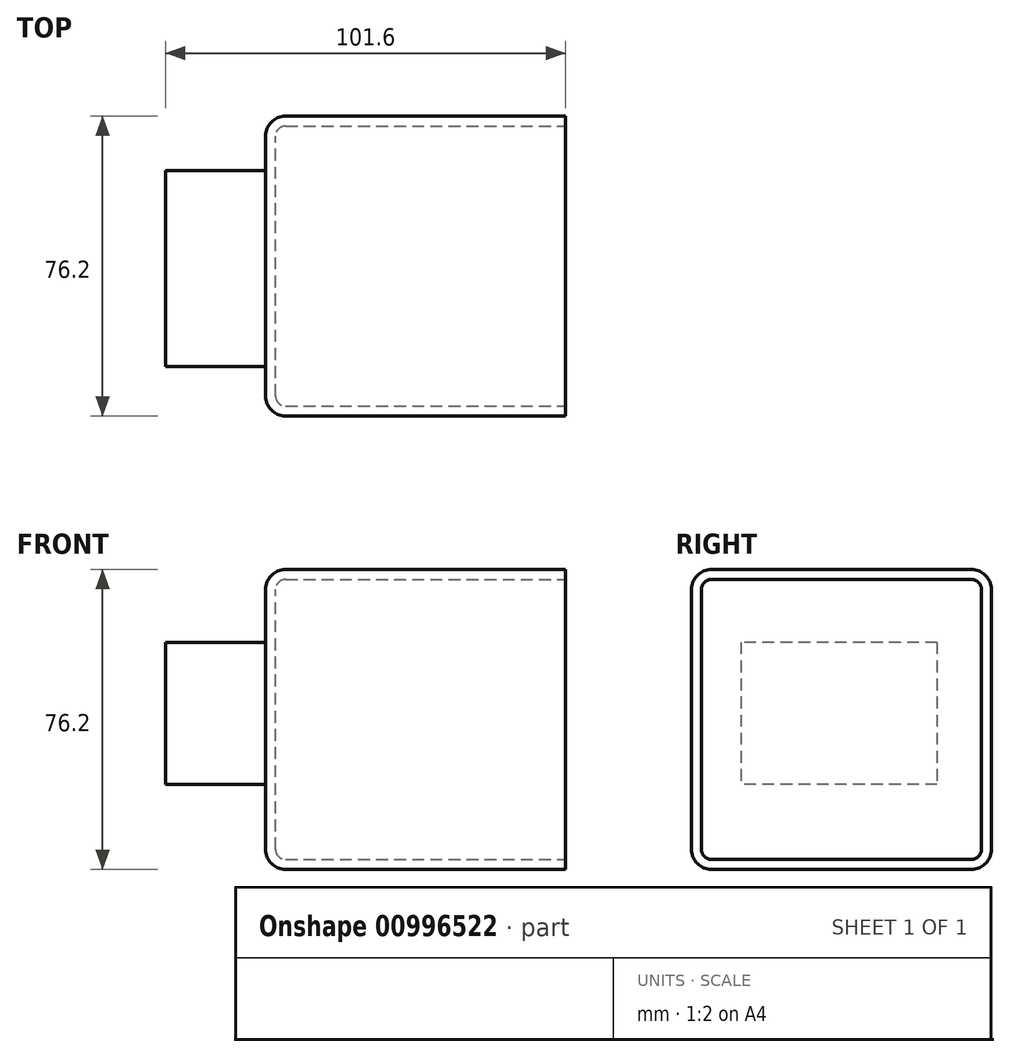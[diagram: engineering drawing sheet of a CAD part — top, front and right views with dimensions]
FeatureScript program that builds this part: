
annotation { "Feature Type Name" : "Feature", "Feature Type Description" : "" }
export const myFeature = defineFeature(function(context is Context, id is Id, definition is map)
    precondition{}
    {
        {
            var Q0;
            Q0=qCreatedBy(makeId("Top.planeOp"),FACE);
            var sketch = newSketch(context, id + "F0", { "sketchPlane" : qUnion([Q0])});
            skLineSegment(sketch, "E0.bottom", {"start": v(0, 0) * mm, "end": v(0, 0) * mm});
            skLineSegment(sketch, "E0.top", {"start": v(0, 0) * mm, "end": v(0, 0) * mm});
            skLineSegment(sketch, "E0.left", {"start": v(0, 0) * mm, "end": v(0, 0) * mm});
            skLineSegment(sketch, "E0.right", {"start": v(0, 0) * mm, "end": v(0, 0) * mm});
            skPoint(sketch, "E0.middle", {"position": v(0, 0) * mm});
            skLineSegment(sketch, "E1.bottom", {"start": v(38.1, 38.1) * mm, "end": v(-38.1, 38.1) * mm});
            skLineSegment(sketch, "E1.top", {"start": v(38.1, -38.1) * mm, "end": v(-38.1, -38.1) * mm});
            skLineSegment(sketch, "E1.left", {"start": v(38.1, 38.1) * mm, "end": v(38.1, -38.1) * mm});
            skLineSegment(sketch, "E1.right", {"start": v(-38.1, 38.1) * mm, "end": v(-38.1, -38.1) * mm});
            skSolve(sketch);
        }
        {
            var Q0;
            Q0=makeQuery(id+"F0.imprint","IMPRINT",FACE,{"disambiguationData":[TD([[makeQuery(id+"F0.imprint","IMPRINT",EDGE,{"derivedFrom":sQuery(id+"F0.wireOp",EDGE,"E1.bottom")}),1.0]])]});
            extrude(context, id + "F1", {"entities" : qUnion([Q0]), "oppositeDirection" : true, "depth" : 76.2 * mm, "offsetDistance" : 25.4 * mm});
        }
        {
            var Q0;
            Q0=makeQuery(id+"F1.opExtrude","CAP_EDGE",EDGE,{"disambiguationData":[OSD([sQuery(id+"F0.wireOp",EDGE,"E1.top")])],"isStart":true});
            var Q1;
            Q1=makeQuery(id+"F1.opExtrude","CAP_EDGE",EDGE,{"disambiguationData":[OSD([sQuery(id+"F0.wireOp",EDGE,"E1.bottom")])],"isStart":true});
            var Q2;
            Q2=makeQuery(id+"F1.opExtrude","CAP_EDGE",EDGE,{"disambiguationData":[OSD([sQuery(id+"F0.wireOp",EDGE,"E1.top")])],"isStart":false});
            var Q3;
            Q3=makeQuery(id+"F1.opExtrude","CAP_EDGE",EDGE,{"disambiguationData":[OSD([sQuery(id+"F0.wireOp",EDGE,"E1.bottom")])],"isStart":false});
            var Q4;
            Q4=makeQuery(id+"F1.opExtrude","CAP_EDGE",EDGE,{"disambiguationData":[OSD([sQuery(id+"F0.wireOp",EDGE,"E1.right")])],"isStart":false});
            var Q5;
            Q5=makeQuery(id+"F1.opExtrude","SWEPT_EDGE",EDGE,{"disambiguationData":[OSD([sQuery(id+"F0.wireOp",EDGE,"E1.bottom"),sQuery(id+"F0.wireOp",EDGE,"E1.right")])]});
            var Q6;
            Q6=makeQuery(id+"F1.opExtrude","CAP_EDGE",EDGE,{"disambiguationData":[OSD([sQuery(id+"F0.wireOp",EDGE,"E1.right")])],"isStart":true});
            var Q7;
            Q7=makeQuery(id+"F1.opExtrude","SWEPT_EDGE",EDGE,{"disambiguationData":[OSD([sQuery(id+"F0.wireOp",EDGE,"E1.top"),sQuery(id+"F0.wireOp",EDGE,"E1.right")])]});
            fillet(context, id + "F2", {"entities" : qUnion([Q0, Q1, Q2, Q3, Q4, Q5, Q6, Q7]), "radius" : 5.08 * mm, "tangentPropagation" : true, "allowEdgeOverflow" : false});
        }
        {
            var Q0;
            Q0=makeQuery(id+"F1.opExtrude","SWEPT_FACE",FACE,{"disambiguationData":[OSD([sQuery(id+"F0.wireOp",EDGE,"E1.left")])]});
            shell(context, id + "F3", {"entities" : qUnion([Q0]), "thickness" : 2.54 * mm});
        }
        {
            var Q0;
            Q0=makeQuery(id+"F1.opExtrude","SWEPT_FACE",FACE,{"disambiguationData":[OSD([sQuery(id+"F0.wireOp",EDGE,"E1.right")])]});
            var sketch = newSketch(context, id + "F4", { "sketchPlane" : qUnion([Q0])});
            skLineSegment(sketch, "E2.bottom", {"start": v(-24.32, -18.5) * mm, "end": v(25.54, -18.5) * mm});
            skLineSegment(sketch, "E2.top", {"start": v(-24.32, -54.65) * mm, "end": v(25.54, -54.65) * mm});
            skLineSegment(sketch, "E2.left", {"start": v(-24.32, -18.5) * mm, "end": v(-24.32, -54.65) * mm});
            skLineSegment(sketch, "E2.right", {"start": v(25.54, -18.5) * mm, "end": v(25.54, -54.65) * mm});
            skSolve(sketch);
        }
        {
            var Q0;
            Q0=makeQuery(id+"F4.imprint","IMPRINT",FACE,{"disambiguationData":[TD([[makeQuery(id+"F4.imprint","IMPRINT",EDGE,{"derivedFrom":sQuery(id+"F4.wireOp",EDGE,"E2.bottom")}),-1.0]])]});
            extrude(context, id + "F5", {"entities" : qUnion([Q0]), "operationType" : NewBodyOperationType.ADD, "depth" : 25.4 * mm, "offsetDistance" : 25.4 * mm});
        }
    });
